# Revit family: QF_ELECTROLUXPROFESSIONAL_1LSNJ5_IC64825_E
name_source: partatom
category: Attrezzature speciali
units: mm (PartAtom-declared; Revit-internal decimal feet)

## family parameters
Basato su piano di lavoro = No
Condiviso = No
Punto di calcolo locali = No
Quota connettore circolare = Usa diametro
Sempre verticale = Sì
Taglio con vuoti quando caricato = No
Tipo di parte = Normale

## types (8) — shared parameters
Cycle = 50 Hz
Depth Actual = 1110 mm  [stored 3.64173 ft]
Height Actual = 1270 mm  [stored 4.16667 ft]
Latent Heat Output = 0.0
Length Actual = 3205 mm  [stored 10.5151 ft]
Modello = IC64825
Phase = 3
Produttore = Electrolux Professional
Sensible Heat Output = 0.0
URL = www.electroluxprofessional.com
Volts = 400 V
Watts = 44500 W
Weight = 860
zero-valued in all types: Gas KW, Prospetto di default, Steam Pounds per Hour

## per-type parameters (varying)
| type | Descrizione | Item Number |
| 9882030165 | IRONER CYLINDER IC64825 2540MM PERFORMANCE EL. CE 400/50/3 DUBIXIUM FR VAC.FEED.TABLE | 1LA22X |
| 9882030257 | IRONER CYLINDER IC64825 2540MM SUPERIOR EL. CE 400/50/3 DUBIXIUM ML FEED ALONE VAC.FEED.TABLE | 1LSPMZ |
| 9882030284 | IRONER CYLINDER IC64825 2540MM ACTIVE EL. CE 400/50/3 6MM SST CYL. FR FEED NOW | 1L0H68 |
| 9882030253 | IRONER CYLINDER IC64825 2540MM ACTIVE EL. CE 400/50/3 6MM SST CYL. ML FEED NOW | 1L828H |
| 9882030166 | IRONER CYLINDER IC64825 2540MM PERFORMANCE EL. CE 400/50/3 DUBIXIUM ML VAC.FEED.TABLE | 1LA22Y |
| 9882030289 | IRONER CYLINDER IC64825 2540MM EL. CE 400/50/3 DUBIXIUM No VAC.FEED.TABLE DIAMMS | 1L0HBC |
| 9882030317 | IRONER CYLINDER IC64825 2540MM SUPERIOR EL. CE 400/50/3 DUBIXIUM FR FEED ALONE VAC.FEED.TABLE | 1LT6DC |
| 9882030293 | IRONER CYLINDER IC64825 2540MM EL. CE 400/50/3 DUBIXIUM SE, DK, FI VAC.FEED.TABLE ANTISTATIC DIAMMS | 1LM09X |

note: [stored X ft] marks values corroborated as IEEE doubles in the binary element streams (Revit-internal decimal feet)

## geometry (parser evidence)
native form markers: Sweep x11
no freeform markers — native parametric forms only
